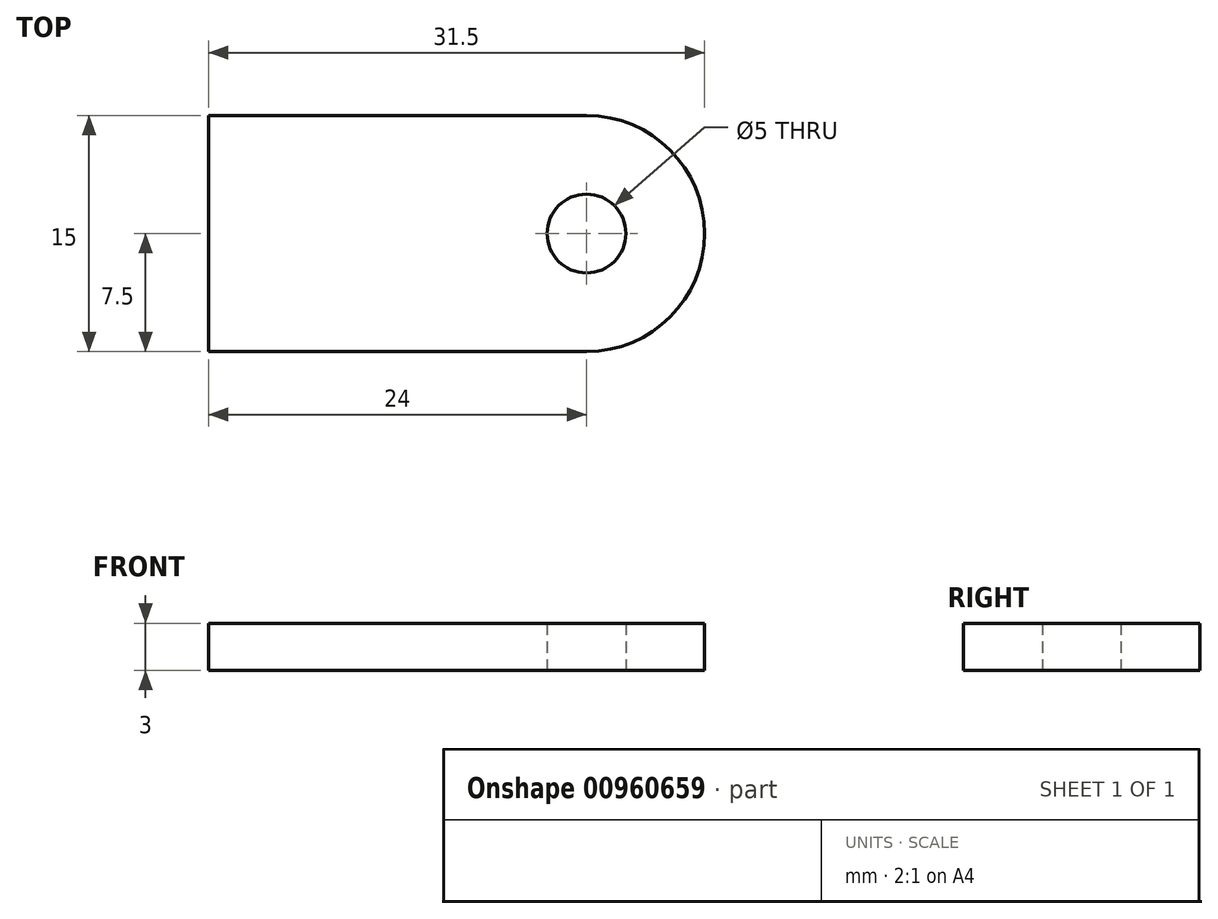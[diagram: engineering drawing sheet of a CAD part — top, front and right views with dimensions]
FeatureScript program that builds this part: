
annotation { "Feature Type Name" : "Feature", "Feature Type Description" : "" }
export const myFeature = defineFeature(function(context is Context, id is Id, definition is map)
    precondition{}
    {
        {
            var Q0;
            Q0=qCreatedBy(makeId("Top.planeOp"),FACE);
            var sketch = newSketch(context, id + "F0", { "sketchPlane" : qUnion([Q0])});
            skLineSegment(sketch, "E0", {"start": v(0, 0) * mm, "end": v(0, -15) * mm});
            skLineSegment(sketch, "E1", {"start": v(0, -15) * mm, "end": v(24, -15) * mm});
            skLineSegment(sketch, "E2", {"start": v(24, 0) * mm, "end": v(0, 0) * mm});
            skLineSegment(sketch, "E3", {"start": v(0, -7.5) * mm, "end": v(24, -7.5) * mm});
            skCircle(sketch, "E4", {"center": v(24, -7.5) * mm, "radius": 2.5 * mm});
            skArc(sketch, "E5", {"start": v(24, -15) * mm, "mid": v(31.5, -7.5) * mm, "end": v(24, 0) * mm});
            skPoint(sketch, "E6.orphan", {"position": v(31.5, 0) * mm});
            skSolve(sketch);
        }
        {
            var Q0;
            Q0 = qSketchRegion(id + "F0", true);
            extrude(context, id + "F1", {"entities" : qUnion([Q0]), "depth" : 3 * mm, "offsetDistance" : 25 * mm});
        }
    });
